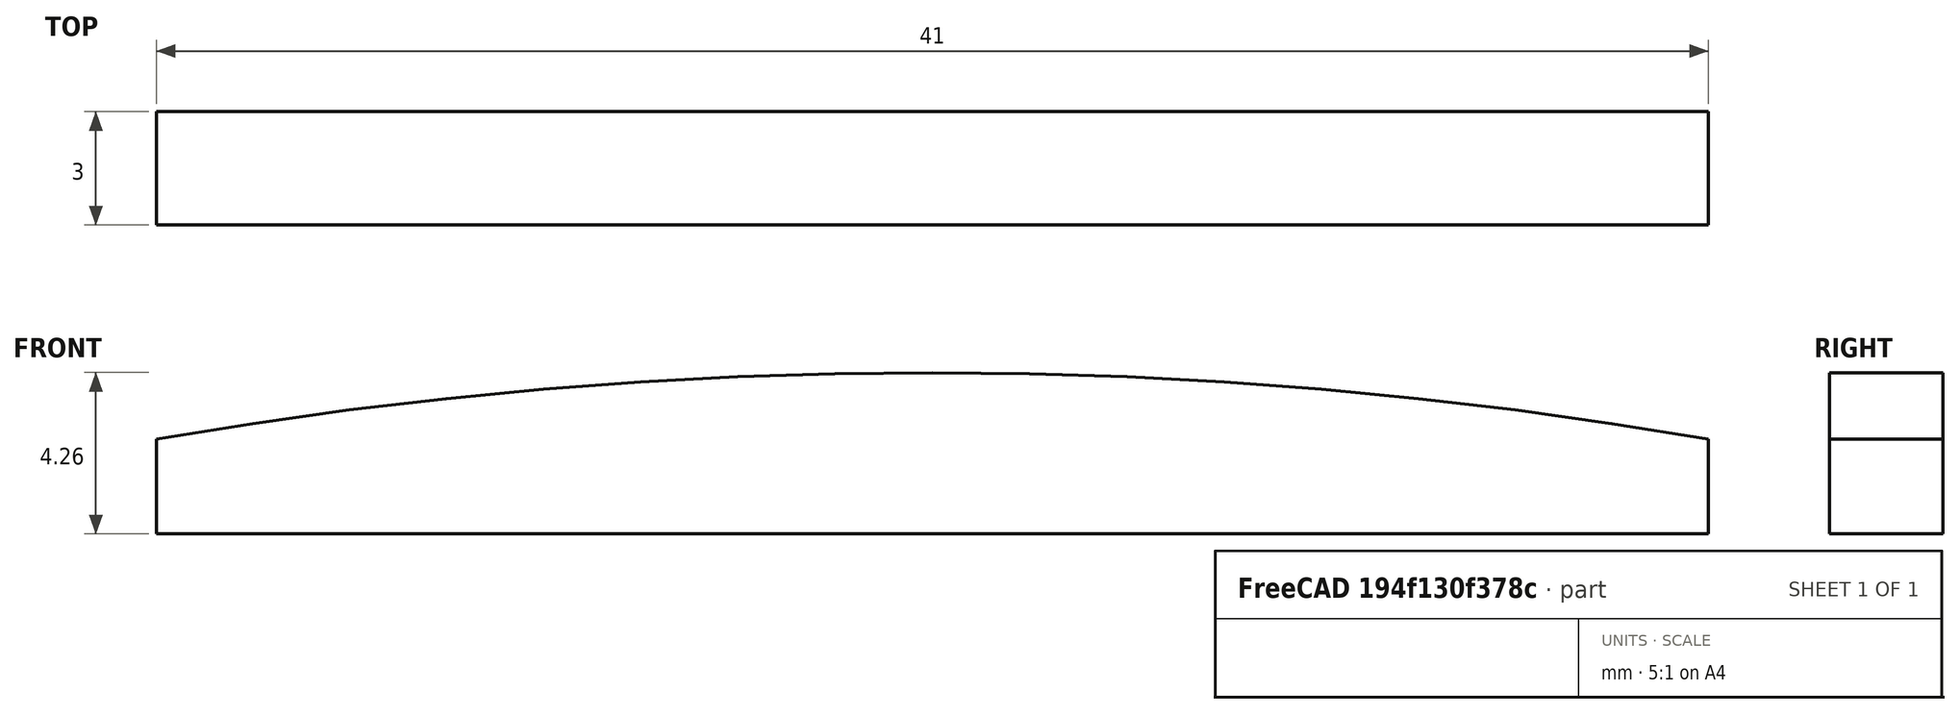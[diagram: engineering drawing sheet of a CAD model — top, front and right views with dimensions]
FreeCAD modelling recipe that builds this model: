
FCSTD DOCUMENT  (FreeCAD 0.19R)
Label: nut
License: All rights reserved
LicenseURL: http://en.wikipedia.org/wiki/All_rights_reserved
objects: Sketcher::SketchObject×1, PartDesign::Pad×1, PartDesign::Body×1
note: 4 computed .brp shape members not serialized (recipe doc carries the construction recipe); baked Part::Feature solids carry a one-line shape summary decoded from their .brp

FEATURE [Sketcher::SketchObject] Sketch
  FullyConstrained = true
  MapMode = 5
  Placement = pos=(0,0,0) rot=(1,0,0;1.5708rad)
  Support = -> [XZ_Plane]
  sketch-geometry (4):
    g0: LineSegment StartX=0 StartY=2.5 StartZ=0 EndX=0 EndY=0 EndZ=0
    g1: LineSegment StartX=0 StartY=0 StartZ=0 EndX=41 EndY=0 EndZ=0
    g2: LineSegment StartX=41 StartY=0 StartZ=0 EndX=41 EndY=2.5 EndZ=0
    g3: ArcOfCircle CenterX=20.5 CenterY=-116.243 CenterZ=0 NormalX=0 NormalY=0 NormalZ=1 AngleXU=0 Radius=120.5 StartAngle=1.39984 EndAngle=1.74175
  constraints (12):
    c: Coincident(g0,g1)
    c: Horizontal(g1)
    c: Coincident(g1,g2)
    c: Coincident(g3,g2)
    c: Coincident(g0,g3)
    c: Coincident(g0,g-1)
    c: Vertical(g0)
    c: Vertical(g2)
    c: Horizontal(g2,g0)
    c: DistanceX(g1,g1) = 41
    c: Diameter(g3) = 241
    c: DistanceY(g2,g2) = 2.5
FEATURE [PartDesign::Pad] Pad
  Direction = (1,1,1)
  Length = 3
  Length2 = 100
  Placement = pos=(0,0,0) rot=(1,0,0;1.5708rad)
  Profile = -> Sketch
  Type = 0
FEATURE [PartDesign::Body] Body
  Group = -> [Sketch,Pad]
  Origin = -> Origin
  Tip = -> Pad
